# Revit family: HERZ-Design-Thermostatkopf M28x1.5 9230
name_source: partatom
category: Rohrzubehör
revit_build: Autodesk Revit 2018 (Build: 20190510_1515(x64)
units: mm (PartAtom-declared; Revit-internal decimal feet)

## family parameters
Arbeitsebenenbasiert = Nein
Beim Laden mit Abzugskörper schneiden = Nein
Bemaßung runder Anschluss = Durchmesser verwenden
Gemeinsam genutzt = Nein
Immer vertikal = Nein
OmniClass-Nummer = 23.65.55.14
OmniClass-Titel = Valves for Liquid Services
Teiletyp = Normal

## types (1)
- HERZ-Design-Thermostatkopf M28x1.5 9230
    Anwendungen = Zur Montage auf allen HERZ-Ventilen, die für thermostatischen Betrieb eingerichtet sind.
    Ausführungen = Heizkörperthermostat mit Flüssigkeitsfühler (Hydrosensor)
mit Stellung „0“, Frostsicherung einstellbar, mit Begrenzung und Blockierung des Sollwertbereiches.
Handradfarbe weiß
    Bestellnummer = 1923006
    Frostsicherung = 6 °C
    Funktionsweise = Der HERZ-Thermostat dient als Fühl- und Regelelement. Durch die Volumsänderung der Flüssigkeitsfüllung im HERZHydrosensor wird die Schubspindel des Ventils bewegt.
    Handrad = Kunststoff, weiß
    Hersteller = HERZ Armaturen Ges.m.b.H.
    S01 = 90 mm  [stored 0.295276 ft]
    S02 = 60 mm  [stored 0.19685 ft]
    Sollwertbereich = 0-30°C
    Sollwertbereich Frostsicherung = 6-30°C
    URL = www.herz-armaturen.at

note: [stored X ft] marks values corroborated as IEEE doubles in the binary element streams (Revit-internal decimal feet)
